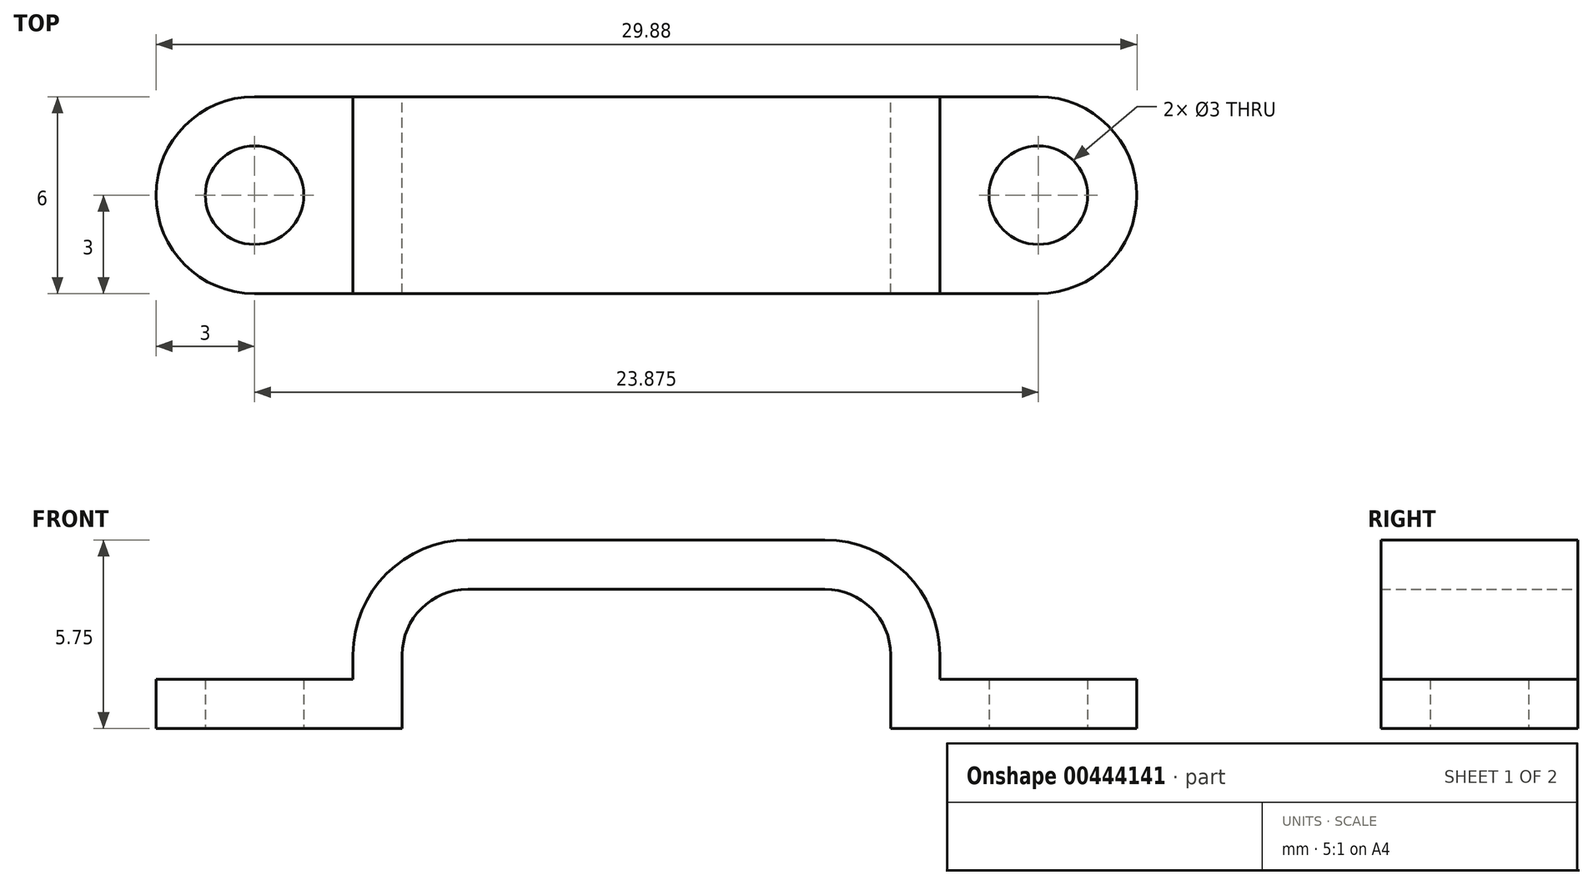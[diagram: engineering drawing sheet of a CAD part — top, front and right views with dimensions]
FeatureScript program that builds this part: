
annotation { "Feature Type Name" : "Feature", "Feature Type Description" : "" }
export const myFeature = defineFeature(function(context is Context, id is Id, definition is map)
    precondition{}
    {
        {
            var Q0;
            Q0=qCreatedBy(makeId("Front.planeOp"),FACE);
            var sketch = newSketch(context, id + "F0", { "sketchPlane" : qUnion([Q0])});
            skLineSegment(sketch, "E0.bottom", {"start": v(0, 0) * mm, "end": v(14.88, 0) * mm});
            skLineSegment(sketch, "E0.top", {"start": v(2, 4.25) * mm, "end": v(12.88, 4.25) * mm});
            skLineSegment(sketch, "E0.left", {"start": v(0, 0) * mm, "end": v(0, 2.25) * mm});
            skLineSegment(sketch, "E0.right", {"start": v(14.88, 0) * mm, "end": v(14.88, 2.25) * mm});
            skPoint(sketch, "E1.visualSharp", {"position": v(0, 4.25) * mm});
            skArc(sketch, "E1.filletArc", {"start": v(2, 4.25) * mm, "mid": v(0.59, 3.66) * mm, "end": v(0, 2.25) * mm});
            skPoint(sketch, "E2.visualSharp", {"position": v(14.88, 4.25) * mm});
            skArc(sketch, "E2.filletArc", {"start": v(14.88, 2.25) * mm, "mid": v(14.29, 3.66) * mm, "end": v(12.88, 4.25) * mm});
            skLineSegment(sketch, "E3.0", {"start": v(16.38, 0) * mm, "end": v(16.38, 2.25) * mm});
            skLineSegment(sketch, "E3.1", {"start": v(-1.5, 0) * mm, "end": v(-1.5, 2.25) * mm});
            skArc(sketch, "E3.2", {"start": v(2, 5.75) * mm, "mid": v(-0.47, 4.72) * mm, "end": v(-1.5, 2.25) * mm});
            skLineSegment(sketch, "E3.3", {"start": v(2, 5.75) * mm, "end": v(12.88, 5.75) * mm});
            skArc(sketch, "E3.4", {"start": v(16.38, 2.25) * mm, "mid": v(15.35, 4.72) * mm, "end": v(12.88, 5.75) * mm});
            skLineSegment(sketch, "E4", {"start": v(-1.5, 0) * mm, "end": v(0, 0) * mm});
            skLineSegment(sketch, "E5", {"start": v(14.88, 0) * mm, "end": v(16.38, 0) * mm});
            skSolve(sketch);
        }
        {
            var Q0;
            Q0=makeQuery(id+"F0.imprint","IMPRINT",FACE,{"disambiguationData":[TD([[makeQuery(id+"F0.imprint","IMPRINT",EDGE,{"derivedFrom":sQuery(id+"F0.wireOp",EDGE,"E0.top")}),1.0]])]});
            extrude(context, id + "F1", {"entities" : qUnion([Q0]), "depth" : 6 * mm});
        }
        {
            var Q0;
            Q0=qCreatedBy(makeId("Top.planeOp"),FACE);
            var sketch = newSketch(context, id + "F2", { "sketchPlane" : qUnion([Q0])});
            skPoint(sketch, "E6.0", {"position": v(16.38, -6) * mm});
            skPoint(sketch, "E7.0", {"position": v(16.38, 0) * mm});
            skPoint(sketch, "E8.0", {"position": v(-1.5, -6) * mm});
            skPoint(sketch, "E9.0", {"position": v(-1.5, 0) * mm});
            skLineSegment(sketch, "E10.bottom", {"start": v(-1.5, 0) * mm, "end": v(-4.5, 0) * mm});
            skLineSegment(sketch, "E10.top", {"start": v(-1.5, -6) * mm, "end": v(-4.5, -6) * mm});
            skLineSegment(sketch, "E10.left", {"start": v(-1.5, 0) * mm, "end": v(-1.5, -6) * mm});
            skLineSegment(sketch, "E10.right", {"start": v(-7.5, -3) * mm, "end": v(-7.5, -3) * mm});
            skPoint(sketch, "E11.visualSharp", {"position": v(-7.5, 0) * mm});
            skArc(sketch, "E11.filletArc", {"start": v(-4.5, 0) * mm, "mid": v(-6.62, -0.88) * mm, "end": v(-7.5, -3) * mm});
            skPoint(sketch, "E12.visualSharp", {"position": v(-7.5, -6) * mm});
            skArc(sketch, "E12.filletArc", {"start": v(-7.5, -3) * mm, "mid": v(-6.62, -5.12) * mm, "end": v(-4.5, -6) * mm});
            skLineSegment(sketch, "E13.bottom", {"start": v(16.38, -6) * mm, "end": v(19.37, -6) * mm});
            skLineSegment(sketch, "E13.top", {"start": v(16.38, 0) * mm, "end": v(19.38, 0) * mm});
            skLineSegment(sketch, "E13.left", {"start": v(16.38, -6) * mm, "end": v(16.38, 0) * mm});
            skLineSegment(sketch, "E13.right", {"start": v(22.38, -3) * mm, "end": v(22.38, -3) * mm});
            skPoint(sketch, "E14.visualSharp", {"position": v(22.38, -6) * mm});
            skArc(sketch, "E14.filletArc", {"start": v(19.37, -6) * mm, "mid": v(21.5, -5.12) * mm, "end": v(22.37, -3) * mm});
            skPoint(sketch, "E15.visualSharp", {"position": v(22.38, 0) * mm});
            skArc(sketch, "E15.filletArc", {"start": v(22.38, -3) * mm, "mid": v(21.5, -0.88) * mm, "end": v(19.38, 0) * mm});
            skCircle(sketch, "E16", {"center": v(-4.5, -3) * mm, "radius": 1.5 * mm});
            skCircle(sketch, "E17", {"center": v(19.37, -3) * mm, "radius": 1.5 * mm});
            skSolve(sketch);
        }
        {
            var Q0;
            Q0=makeQuery(id+"F2.imprint","IMPRINT",FACE,{"disambiguationData":[TD([[makeQuery(id+"F2.imprint","IMPRINT",EDGE,{"derivedFrom":sQuery(id+"F2.wireOp",EDGE,"E10.bottom")}),1.0]])]});
            var Q1;
            Q1=makeQuery(id+"F2.imprint","IMPRINT",FACE,{"disambiguationData":[TD([[makeQuery(id+"F2.imprint","IMPRINT",EDGE,{"derivedFrom":sQuery(id+"F2.wireOp",EDGE,"E13.bottom")}),1.0]])]});
            extrude(context, id + "F3", {"entities" : qUnion([Q0, Q1]), "operationType" : NewBodyOperationType.ADD, "depth" : 1.5 * mm});
        }
    });
